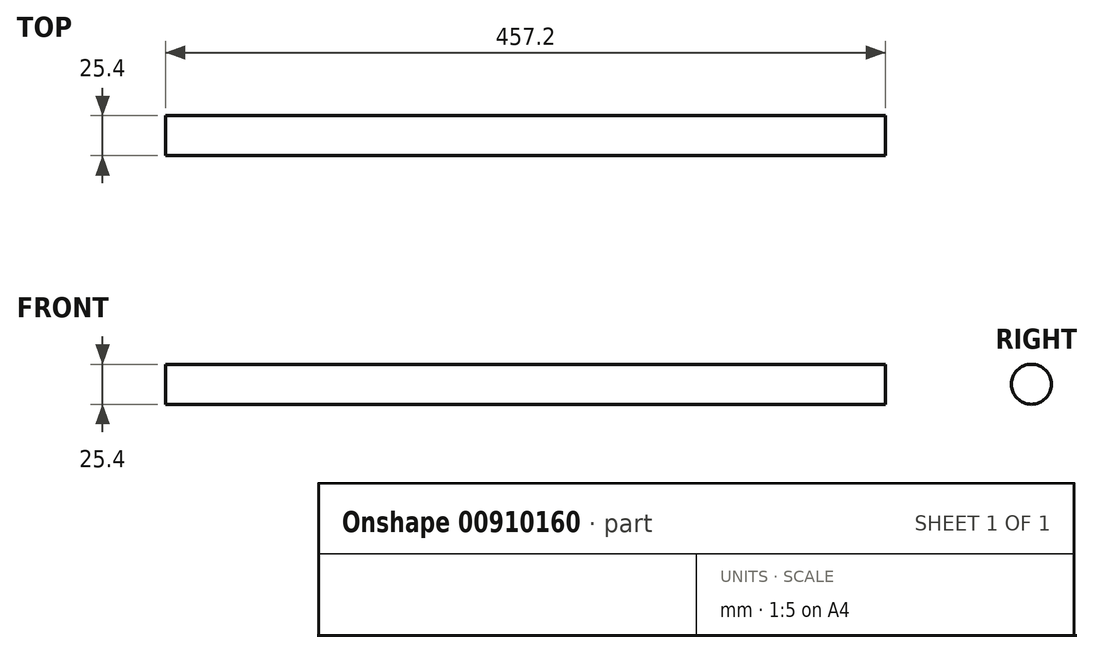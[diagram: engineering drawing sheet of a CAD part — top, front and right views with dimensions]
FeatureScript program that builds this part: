
annotation { "Feature Type Name" : "Feature", "Feature Type Description" : "" }
export const myFeature = defineFeature(function(context is Context, id is Id, definition is map)
    precondition{}
    {
        {
            var Q0;
            Q0=qCreatedBy(makeId("Right.planeOp"),FACE);
            var sketch = newSketch(context, id + "F0", { "sketchPlane" : qUnion([Q0])});
            skCircle(sketch, "E0", {"center": v(0, 0) * mm, "radius": 12.7 * mm});
            skSolve(sketch);
        }
        {
            var Q0;
            Q0 = qSketchRegion(id + "F0", true);
            extrude(context, id + "F1", {"entities" : qUnion([Q0]), "endBound" : BoundingType.SYMMETRIC, "depth" : 457.2 * mm, "offsetDistance" : 25.4 * mm});
        }
    });
